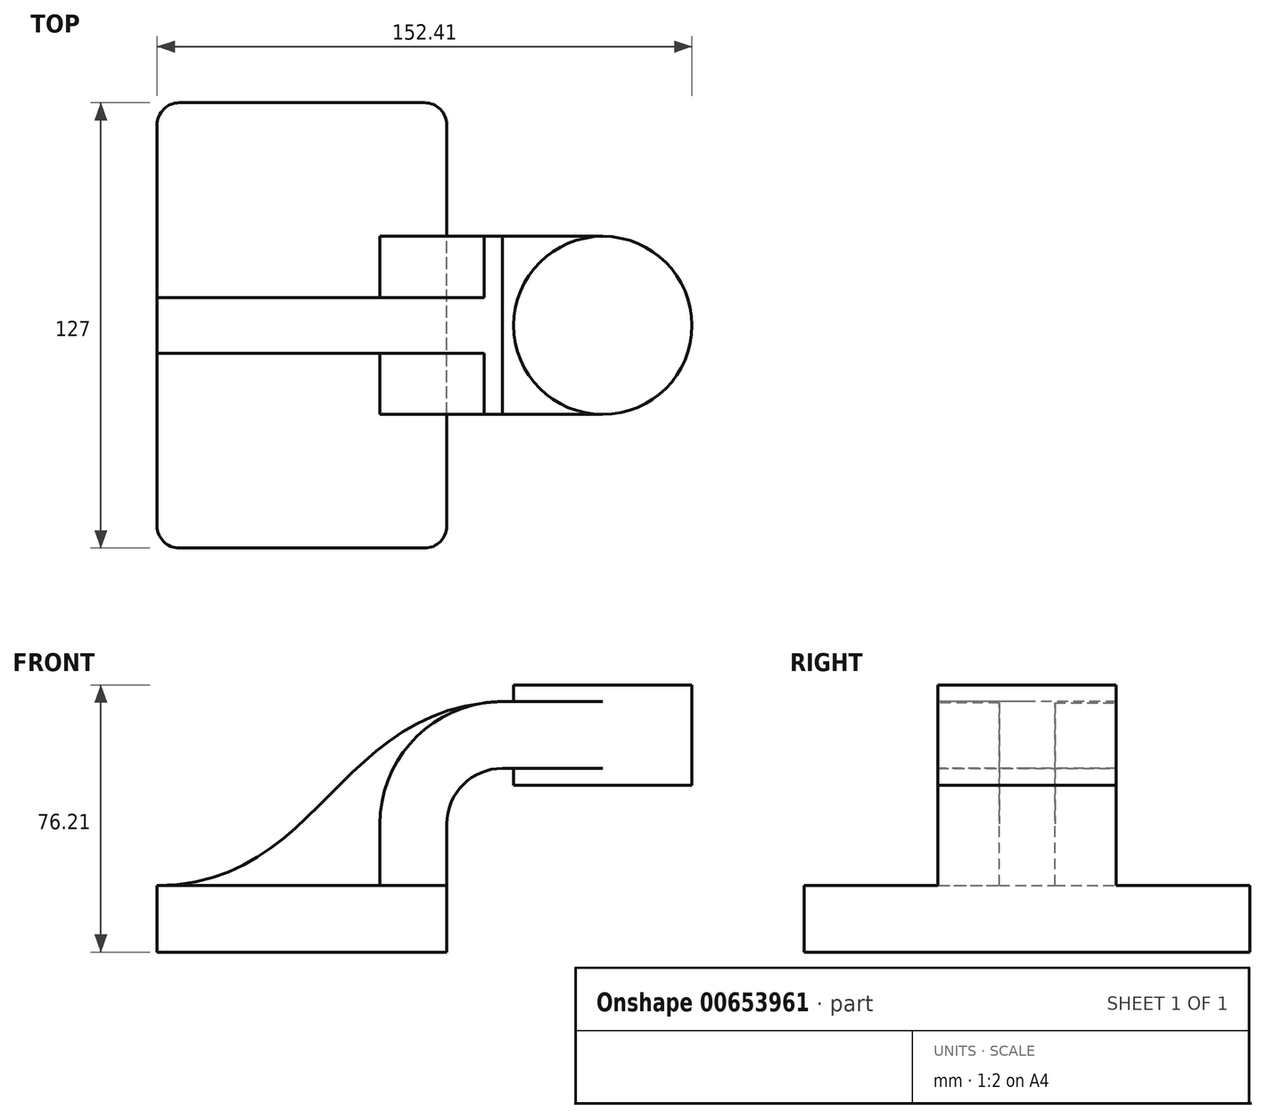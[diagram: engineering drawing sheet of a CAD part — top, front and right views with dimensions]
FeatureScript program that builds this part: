
annotation { "Feature Type Name" : "Feature", "Feature Type Description" : "" }
export const myFeature = defineFeature(function(context is Context, id is Id, definition is map)
    precondition{}
    {
        {
            var Q0;
            Q0=qCreatedBy(makeId("Front.planeOp"),FACE);
            var sketch = newSketch(context, id + "F0", { "sketchPlane" : qUnion([Q0])});
            skLineSegment(sketch, "E0.bottom", {"start": v(41.27, 9.53) * mm, "end": v(-41.28, 9.53) * mm});
            skLineSegment(sketch, "E0.top", {"start": v(41.28, -9.52) * mm, "end": v(-41.27, -9.52) * mm});
            skLineSegment(sketch, "E0.left", {"start": v(41.27, 9.53) * mm, "end": v(41.28, -9.52) * mm});
            skLineSegment(sketch, "E0.right", {"start": v(-41.28, 9.53) * mm, "end": v(-41.27, -9.52) * mm});
            skPoint(sketch, "E0.middle", {"position": v(0, 0) * mm});
            skLineSegment(sketch, "E1.bottom", {"start": v(60.33, 38.1) * mm, "end": v(111.13, 38.1) * mm});
            skLineSegment(sketch, "E1.top", {"start": v(60.32, 66.68) * mm, "end": v(111.12, 66.68) * mm});
            skLineSegment(sketch, "E1.left", {"start": v(60.33, 38.1) * mm, "end": v(60.32, 66.68) * mm});
            skLineSegment(sketch, "E1.right", {"start": v(111.13, 38.1) * mm, "end": v(111.12, 66.68) * mm});
            skPoint(sketch, "E1.middle", {"position": v(85.72, 52.39) * mm});
            skLineSegment(sketch, "E2", {"start": v(41.27, 9.53) * mm, "end": v(41.27, 27) * mm});
            skArc(sketch, "E3", {"start": v(41.27, 27) * mm, "mid": v(45.92, 38.23) * mm, "end": v(57.15, 42.88) * mm});
            skLineSegment(sketch, "E4", {"start": v(57.15, 42.88) * mm, "end": v(101.35, 42.88) * mm});
            skLineSegment(sketch, "E5.0", {"start": v(57.15, 61.93) * mm, "end": v(101.35, 61.93) * mm});
            skArc(sketch, "E5.1", {"start": v(22.22, 27) * mm, "mid": v(32.45, 51.7) * mm, "end": v(57.15, 61.93) * mm});
            skLineSegment(sketch, "E5.2", {"start": v(22.22, 9.53) * mm, "end": v(22.22, 27) * mm});
            skFitSpline(sketch, "E6", {"points": [v(-41.28, 9.52) * mm, v(57.15, 61.93) * mm], "startDerivative": vector(140.51, 0) * mm, "endDerivative": vector(142.13, 4.85) * mm});
            skLineSegment(sketch, "E7", {"start": v(85.73, 38.1) * mm, "end": v(85.72, 66.68) * mm});
            skSolve(sketch);
        }
        {
            var Q0;
            Q0=makeQuery(id+"F0.imprint","IMPRINT",FACE,{"disambiguationData":[TD([[makeQuery(id+"F0.imprint","IMPRINT",EDGE,{"derivedFrom":sQuery(id+"F0.wireOp",EDGE,"E0.top")}),-1.0]])]});
            extrude(context, id + "F1", {"entities" : qUnion([Q0]), "endBound" : BoundingType.SYMMETRIC, "depth" : 127 * mm, "offsetDistance" : 25.4 * mm});
        }
        {
            var Q0;
            {var subQ1=sQuery(id+"F0.wireOp",EDGE,"E2");Q0=makeQuery(id+"F0.imprint","IMPRINT",FACE,{"disambiguationData":[TD([[makeQuery(id+"F0.imprint","IMPRINT",EDGE,{"derivedFrom":subQ1}),1.0]])]});}
            var Q1;
            {var subQ0=sQuery(id+"F0.wireOp",EDGE,"E4");var subQ1=sQuery(id+"F0.wireOp",EDGE,"E1.left");var subQ2=makeQuery(id+"F0.imprint","INTERSECT",VERTEX,{"derivedFrom":[subQ1,subQ0]});Q1=makeQuery(id+"F0.imprint","IMPRINT",FACE,{"disambiguationData":[TD([[makeQuery(id+"F0.imprint","IMPRINT",EDGE,{"disambiguationData":[TD([[subQ2,-1.0]])],"derivedFrom":subQ1}),-1.0]])]});}
            extrude(context, id + "F2", {"entities" : qUnion([Q0, Q1]), "operationType" : NewBodyOperationType.ADD, "endBound" : BoundingType.SYMMETRIC, "depth" : 50.8 * mm, "offsetDistance" : 25.4 * mm});
        }
        {
            var Q0;
            {var subQ3=sQuery(id+"F0.wireOp",EDGE,"E5.2");Q0=makeQuery(id+"F0.imprint","IMPRINT",FACE,{"disambiguationData":[TD([[makeQuery(id+"F0.imprint","IMPRINT",EDGE,{"derivedFrom":subQ3}),1.0]])]});}
            extrude(context, id + "F3", {"entities" : qUnion([Q0]), "operationType" : NewBodyOperationType.ADD, "endBound" : BoundingType.SYMMETRIC, "depth" : 15.88 * mm, "offsetDistance" : 25.4 * mm});
        }
        {
            var Q0;
            {var subQ4=sQuery(id+"F0.wireOp",EDGE,"E1.right");Q0=makeQuery(id+"F0.imprint","IMPRINT",FACE,{"disambiguationData":[TD([[makeQuery(id+"F0.imprint","IMPRINT",EDGE,{"derivedFrom":subQ4}),1.0]])]});}
            var Q1;
            Q1=sQuery(id+"F0.wireOp",EDGE,"E7");
            revolve(context, id + "F4", {"operationType" : NewBodyOperationType.ADD, "entities" : qUnion([Q0]), "axis" : qUnion([Q1]), "revolveType" : RevolveType.FULL});
        }
        {
            var Q0;
            Q0=makeQuery(id+"F1.opExtrude","CAP_EDGE",EDGE,{"disambiguationData":[OSD([sQuery(id+"F0.wireOp",EDGE,"E0.left")])],"isStart":false});
            var Q1;
            Q1=makeQuery(id+"F1.opExtrude","CAP_EDGE",EDGE,{"disambiguationData":[OSD([sQuery(id+"F0.wireOp",EDGE,"E0.left")])],"isStart":true});
            var Q2;
            Q2=makeQuery(id+"F1.opExtrude","CAP_EDGE",EDGE,{"disambiguationData":[OSD([sQuery(id+"F0.wireOp",EDGE,"E0.right")])],"isStart":true});
            var Q3;
            Q3=makeQuery(id+"F1.opExtrude","CAP_EDGE",EDGE,{"disambiguationData":[OSD([sQuery(id+"F0.wireOp",EDGE,"E0.right")])],"isStart":false});
            fillet(context, id + "F5", {"entities" : qUnion([Q0, Q1, Q2, Q3]), "radius" : 6.35 * mm, "tangentPropagation" : true, "allowEdgeOverflow" : false});
        }
    });
